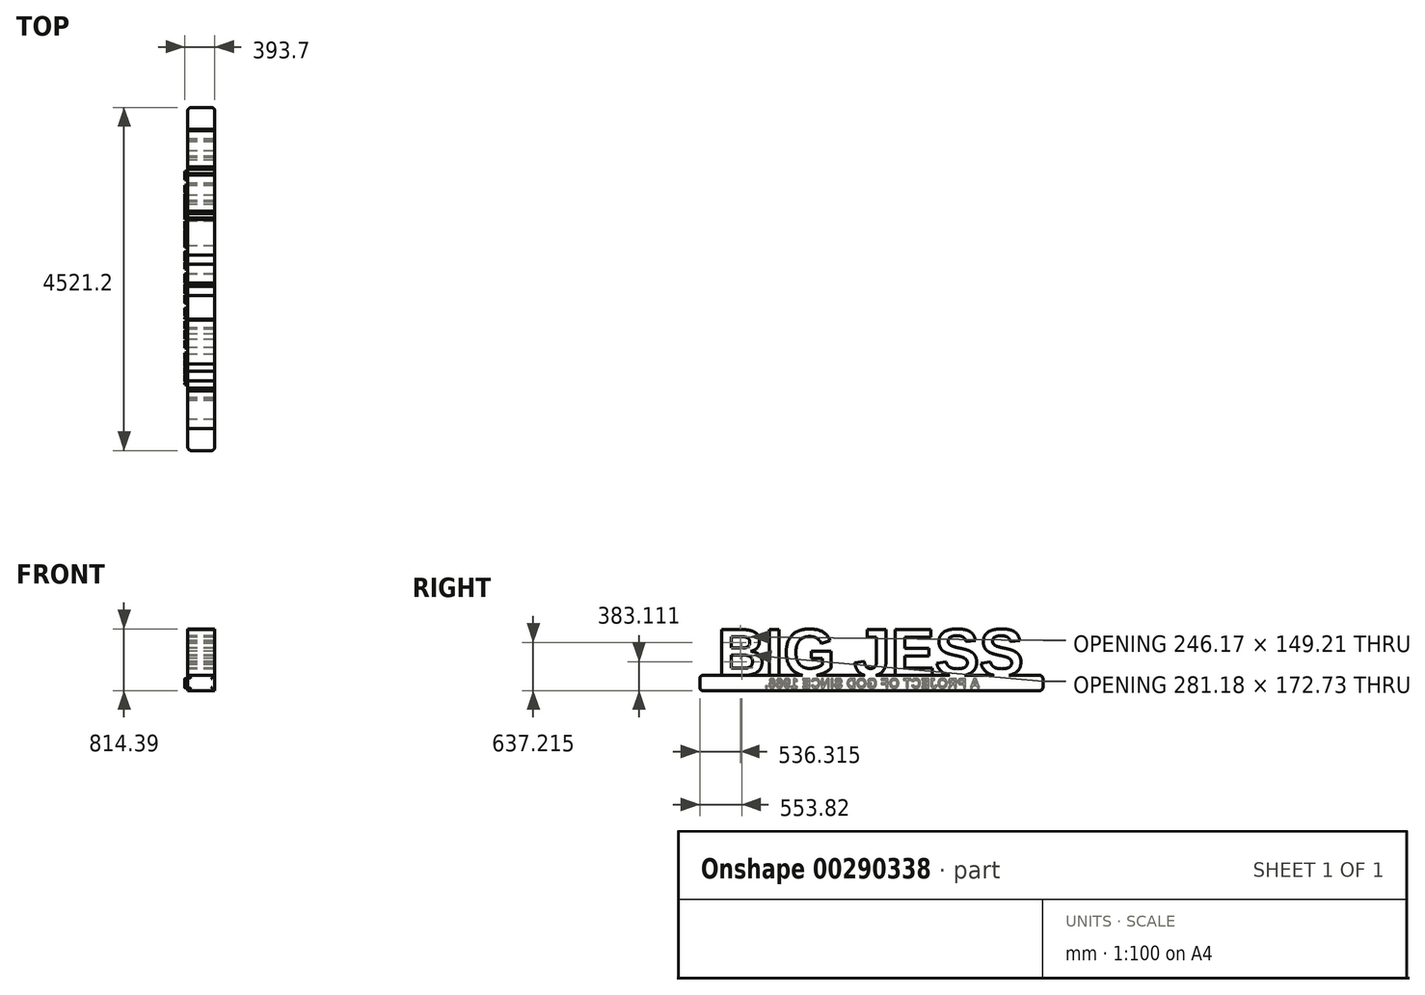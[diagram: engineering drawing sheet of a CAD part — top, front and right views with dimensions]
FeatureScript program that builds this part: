
annotation { "Feature Type Name" : "Feature", "Feature Type Description" : "" }
export const myFeature = defineFeature(function(context is Context, id is Id, definition is map)
    precondition{}
    {
        {
            var Q0;
            Q0=qCreatedBy(makeId("Right.planeOp"),FACE);
            var sketch = newSketch(context, id + "F0", { "sketchPlane" : qUnion([Q0])});
            skText(sketch, "E0", { "text": "BIG JESS", "fontName": "Arimo-Bold.ttf"});
            skLineSegment(sketch, "E1", {"start": v(-2808.47, 1181.62) * mm, "end": v(-2808.47, 978.42) * mm});
            skLineSegment(sketch, "E2", {"start": v(-2808.47, 978.42) * mm, "end": v(1712.73, 978.42) * mm});
            skLineSegment(sketch, "E3", {"start": v(1712.73, 978.42) * mm, "end": v(1712.73, 1181.62) * mm});
            skLineSegment(sketch, "E4", {"start": v(-2808.47, 1181.62) * mm, "end": v(1712.73, 1181.62) * mm});
            const initialGuessF0  = {"E0": [-2.57987, 1.18162, 1, 0, 0.6302]};
            skSetInitialGuess(sketch, initialGuessF0);
            skSolve(sketch);
        }
        {
            var Q0;
            Q0 = qSketchRegion(id + "F0", true);
            extrude(context, id + "F1", {"entities" : qUnion([Q0]), "depth" : 355.6 * mm});
        }
        {
            var Q0;
            Q0=makeQuery(id+"F1.opExtrude","CAP_FACE",FACE,{"disambiguationData":[OSD([sQuery(id+"F0.wireOp",EDGE,"E0.sketch_text.stroke-0"),sQuery(id+"F0.wireOp",EDGE,"E0.sketch_text.stroke-1"),sQuery(id+"F0.wireOp",EDGE,"E0.sketch_text.stroke-3"),sQuery(id+"F0.wireOp",EDGE,"E0.sketch_text.stroke-4"),sQuery(id+"F0.wireOp",EDGE,"E0.sketch_text.stroke-5"),sQuery(id+"F0.wireOp",EDGE,"E0.sketch_text.stroke-6"),sQuery(id+"F0.wireOp",EDGE,"E0.sketch_text.stroke-7"),sQuery(id+"F0.wireOp",EDGE,"E0.sketch_text.stroke-8"),sQuery(id+"F0.wireOp",EDGE,"E0.sketch_text.stroke-9"),sQuery(id+"F0.wireOp",EDGE,"E0.sketch_text.stroke-10"),sQuery(id+"F0.wireOp",EDGE,"E0.sketch_text.stroke-11"),sQuery(id+"F0.wireOp",EDGE,"E0.sketch_text.stroke-12"),sQuery(id+"F0.wireOp",EDGE,"E0.sketch_text.stroke-13"),sQuery(id+"F0.wireOp",EDGE,"E0.sketch_text.stroke-14"),sQuery(id+"F0.wireOp",EDGE,"E0.sketch_text.stroke-15"),sQuery(id+"F0.wireOp",EDGE,"E0.sketch_text.stroke-16"),sQuery(id+"F0.wireOp",EDGE,"E0.sketch_text.stroke-17"),sQuery(id+"F0.wireOp",EDGE,"E0.sketch_text.stroke-18"),sQuery(id+"F0.wireOp",EDGE,"E0.sketch_text.stroke-19"),sQuery(id+"F0.wireOp",EDGE,"E0.sketch_text.stroke-20"),sQuery(id+"F0.wireOp",EDGE,"E0.sketch_text.stroke-21"),sQuery(id+"F0.wireOp",EDGE,"E0.sketch_text.stroke-22"),sQuery(id+"F0.wireOp",EDGE,"E0.sketch_text.stroke-23"),sQuery(id+"F0.wireOp",EDGE,"E0.sketch_text.stroke-24"),sQuery(id+"F0.wireOp",EDGE,"E0.sketch_text.stroke-25"),sQuery(id+"F0.wireOp",EDGE,"E0.sketch_text.stroke-26"),sQuery(id+"F0.wireOp",EDGE,"E0.sketch_text.stroke-28"),sQuery(id+"F0.wireOp",EDGE,"E0.sketch_text.stroke-29"),sQuery(id+"F0.wireOp",EDGE,"E0.sketch_text.stroke-30"),sQuery(id+"F0.wireOp",EDGE,"E0.sketch_text.stroke-31"),sQuery(id+"F0.wireOp",EDGE,"E0.sketch_text.stroke-32"),sQuery(id+"F0.wireOp",EDGE,"E0.sketch_text.stroke-33"),sQuery(id+"F0.wireOp",EDGE,"E0.sketch_text.stroke-34"),sQuery(id+"F0.wireOp",EDGE,"E0.sketch_text.stroke-35"),sQuery(id+"F0.wireOp",EDGE,"E0.sketch_text.stroke-36"),sQuery(id+"F0.wireOp",EDGE,"E0.sketch_text.stroke-37"),sQuery(id+"F0.wireOp",EDGE,"E0.sketch_text.stroke-38"),sQuery(id+"F0.wireOp",EDGE,"E0.sketch_text.stroke-39"),sQuery(id+"F0.wireOp",EDGE,"E0.sketch_text.stroke-40"),sQuery(id+"F0.wireOp",EDGE,"E0.sketch_text.stroke-41"),sQuery(id+"F0.wireOp",EDGE,"E0.sketch_text.stroke-42"),sQuery(id+"F0.wireOp",EDGE,"E0.sketch_text.stroke-43"),sQuery(id+"F0.wireOp",EDGE,"E0.sketch_text.stroke-44"),sQuery(id+"F0.wireOp",EDGE,"E0.sketch_text.stroke-45"),sQuery(id+"F0.wireOp",EDGE,"E0.sketch_text.stroke-46"),sQuery(id+"F0.wireOp",EDGE,"E0.sketch_text.stroke-47"),sQuery(id+"F0.wireOp",EDGE,"E0.sketch_text.stroke-48"),sQuery(id+"F0.wireOp",EDGE,"E0.sketch_text.stroke-49"),sQuery(id+"F0.wireOp",EDGE,"E0.sketch_text.stroke-50"),sQuery(id+"F0.wireOp",EDGE,"E0.sketch_text.stroke-51"),sQuery(id+"F0.wireOp",EDGE,"E0.sketch_text.stroke-52"),sQuery(id+"F0.wireOp",EDGE,"E0.sketch_text.stroke-53"),sQuery(id+"F0.wireOp",EDGE,"E0.sketch_text.stroke-54"),sQuery(id+"F0.wireOp",EDGE,"E0.sketch_text.stroke-55"),sQuery(id+"F0.wireOp",EDGE,"E0.sketch_text.stroke-56"),sQuery(id+"F0.wireOp",EDGE,"E0.sketch_text.stroke-57"),sQuery(id+"F0.wireOp",EDGE,"E0.sketch_text.stroke-58"),sQuery(id+"F0.wireOp",EDGE,"E0.sketch_text.stroke-59"),sQuery(id+"F0.wireOp",EDGE,"E0.sketch_text.stroke-60"),sQuery(id+"F0.wireOp",EDGE,"E0.sketch_text.stroke-61"),sQuery(id+"F0.wireOp",EDGE,"E0.sketch_text.stroke-62"),sQuery(id+"F0.wireOp",EDGE,"E0.sketch_text.stroke-63"),sQuery(id+"F0.wireOp",EDGE,"E0.sketch_text.stroke-64"),sQuery(id+"F0.wireOp",EDGE,"E0.sketch_text.stroke-65"),sQuery(id+"F0.wireOp",EDGE,"E0.sketch_text.stroke-66"),sQuery(id+"F0.wireOp",EDGE,"E0.sketch_text.stroke-67"),sQuery(id+"F0.wireOp",EDGE,"E0.sketch_text.stroke-68"),sQuery(id+"F0.wireOp",EDGE,"E0.sketch_text.stroke-69"),sQuery(id+"F0.wireOp",EDGE,"E0.sketch_text.stroke-70"),sQuery(id+"F0.wireOp",EDGE,"E0.sketch_text.stroke-71"),sQuery(id+"F0.wireOp",EDGE,"E0.sketch_text.stroke-72"),sQuery(id+"F0.wireOp",EDGE,"E0.sketch_text.stroke-73"),sQuery(id+"F0.wireOp",EDGE,"E0.sketch_text.stroke-75"),sQuery(id+"F0.wireOp",EDGE,"E0.sketch_text.stroke-76"),sQuery(id+"F0.wireOp",EDGE,"E0.sketch_text.stroke-77"),sQuery(id+"F0.wireOp",EDGE,"E0.sketch_text.stroke-78"),sQuery(id+"F0.wireOp",EDGE,"E0.sketch_text.stroke-79"),sQuery(id+"F0.wireOp",EDGE,"E0.sketch_text.stroke-80"),sQuery(id+"F0.wireOp",EDGE,"E0.sketch_text.stroke-81"),sQuery(id+"F0.wireOp",EDGE,"E0.sketch_text.stroke-82"),sQuery(id+"F0.wireOp",EDGE,"E0.sketch_text.stroke-83"),sQuery(id+"F0.wireOp",EDGE,"E0.sketch_text.stroke-84"),sQuery(id+"F0.wireOp",EDGE,"E0.sketch_text.stroke-85"),sQuery(id+"F0.wireOp",EDGE,"E0.sketch_text.stroke-86"),sQuery(id+"F0.wireOp",EDGE,"E0.sketch_text.stroke-87"),sQuery(id+"F0.wireOp",EDGE,"E0.sketch_text.stroke-88"),sQuery(id+"F0.wireOp",EDGE,"E0.sketch_text.stroke-89"),sQuery(id+"F0.wireOp",EDGE,"E0.sketch_text.stroke-90"),sQuery(id+"F0.wireOp",EDGE,"E0.sketch_text.stroke-91"),sQuery(id+"F0.wireOp",EDGE,"E0.sketch_text.stroke-92"),sQuery(id+"F0.wireOp",EDGE,"E0.sketch_text.stroke-93"),sQuery(id+"F0.wireOp",EDGE,"E0.sketch_text.stroke-94"),sQuery(id+"F0.wireOp",EDGE,"E0.sketch_text.stroke-95"),sQuery(id+"F0.wireOp",EDGE,"E0.sketch_text.stroke-96"),sQuery(id+"F0.wireOp",EDGE,"E0.sketch_text.stroke-97"),sQuery(id+"F0.wireOp",EDGE,"E0.sketch_text.stroke-98"),sQuery(id+"F0.wireOp",EDGE,"E0.sketch_text.stroke-99"),sQuery(id+"F0.wireOp",EDGE,"E0.sketch_text.stroke-100"),sQuery(id+"F0.wireOp",EDGE,"E0.sketch_text.stroke-101"),sQuery(id+"F0.wireOp",EDGE,"E0.sketch_text.stroke-102"),sQuery(id+"F0.wireOp",EDGE,"E0.sketch_text.stroke-103"),sQuery(id+"F0.wireOp",EDGE,"E0.sketch_text.stroke-104"),sQuery(id+"F0.wireOp",EDGE,"E0.sketch_text.stroke-105"),sQuery(id+"F0.wireOp",EDGE,"E0.sketch_text.stroke-106"),sQuery(id+"F0.wireOp",EDGE,"E0.sketch_text.stroke-107"),sQuery(id+"F0.wireOp",EDGE,"E0.sketch_text.stroke-108"),sQuery(id+"F0.wireOp",EDGE,"E0.sketch_text.stroke-109"),sQuery(id+"F0.wireOp",EDGE,"E0.sketch_text.stroke-110"),sQuery(id+"F0.wireOp",EDGE,"E0.sketch_text.stroke-111"),sQuery(id+"F0.wireOp",EDGE,"E0.sketch_text.stroke-112"),sQuery(id+"F0.wireOp",EDGE,"E0.sketch_text.stroke-113"),sQuery(id+"F0.wireOp",EDGE,"E0.sketch_text.stroke-114"),sQuery(id+"F0.wireOp",EDGE,"E0.sketch_text.stroke-115"),sQuery(id+"F0.wireOp",EDGE,"E0.sketch_text.stroke-116"),sQuery(id+"F0.wireOp",EDGE,"E0.sketch_text.stroke-117"),sQuery(id+"F0.wireOp",EDGE,"E0.sketch_text.stroke-118"),sQuery(id+"F0.wireOp",EDGE,"E0.sketch_text.stroke-119"),sQuery(id+"F0.wireOp",EDGE,"E0.sketch_text.stroke-120"),sQuery(id+"F0.wireOp",EDGE,"E0.sketch_text.stroke-121"),sQuery(id+"F0.wireOp",EDGE,"E0.sketch_text.stroke-122"),sQuery(id+"F0.wireOp",EDGE,"E0.sketch_text.stroke-123"),sQuery(id+"F0.wireOp",EDGE,"E0.sketch_text.stroke-124"),sQuery(id+"F0.wireOp",EDGE,"E0.sketch_text.stroke-125"),sQuery(id+"F0.wireOp",EDGE,"E0.sketch_text.stroke-126"),sQuery(id+"F0.wireOp",EDGE,"E0.sketch_text.stroke-127"),sQuery(id+"F0.wireOp",EDGE,"E0.sketch_text.stroke-128"),sQuery(id+"F0.wireOp",EDGE,"E0.sketch_text.stroke-129"),sQuery(id+"F0.wireOp",EDGE,"E0.sketch_text.stroke-130"),sQuery(id+"F0.wireOp",EDGE,"E0.sketch_text.stroke-131"),sQuery(id+"F0.wireOp",EDGE,"E0.sketch_text.stroke-132"),sQuery(id+"F0.wireOp",EDGE,"E0.sketch_text.stroke-133"),sQuery(id+"F0.wireOp",EDGE,"E0.sketch_text.stroke-134"),sQuery(id+"F0.wireOp",EDGE,"E0.sketch_text.stroke-135"),sQuery(id+"F0.wireOp",EDGE,"E0.sketch_text.stroke-136"),sQuery(id+"F0.wireOp",EDGE,"E1"),sQuery(id+"F0.wireOp",EDGE,"E2"),sQuery(id+"F0.wireOp",EDGE,"E3"),sQuery(id+"F0.wireOp",EDGE,"E4")])],"isStart":true});
            var sketch = newSketch(context, id + "F2", { "sketchPlane" : qUnion([Q0])});
            skText(sketch, "E5", { "text": "A PROJECT OF GOD SINCE 1966.", "fontName": "Arimo-Bold.ttf"});
            const initialGuessF2  = {"E5": [-0.87961, 1.01652, 1, 0, 0.127]};
            skSetInitialGuess(sketch, initialGuessF2);
            skSolve(sketch);
        }
        {
            var Q0;
            Q0 = qSketchRegion(id + "F2", true);
            extrude(context, id + "F3", {"entities" : qUnion([Q0]), "operationType" : NewBodyOperationType.ADD, "depth" : 38.1 * mm});
        }
        {
            var Q0;
            Q0=makeQuery(id+"F1.opExtrude","SWEPT_FACE",FACE,{"disambiguationData":[OSD([sQuery(id+"F0.wireOp",EDGE,"E1")])]});
            fillet(context, id + "F4", {"entities" : qUnion([Q0]), "radius" : 45.72 * mm, "tangentPropagation" : true, "allowEdgeOverflow" : false});
        }
        {
            var Q0;
            Q0=makeQuery(id+"F1.opExtrude","SWEPT_FACE",FACE,{"disambiguationData":[OSD([sQuery(id+"F0.wireOp",EDGE,"E3")])]});
            fillet(context, id + "F5", {"entities" : qUnion([Q0]), "radius" : 45.72 * mm, "tangentPropagation" : true, "allowEdgeOverflow" : false});
        }
    });
